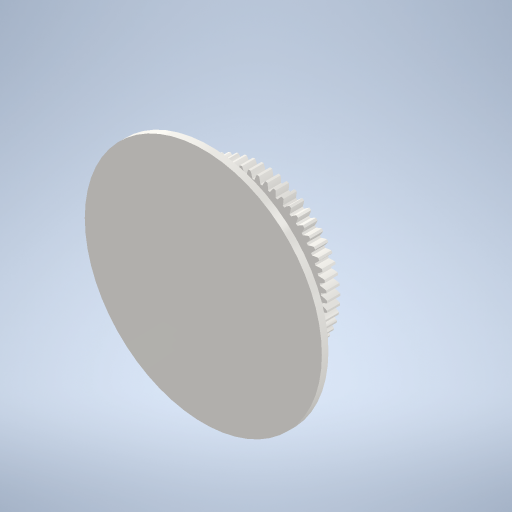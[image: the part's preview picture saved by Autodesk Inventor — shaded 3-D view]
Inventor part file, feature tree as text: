
AUTODESK INVENTOR PART (.ipt)
format: ipt  version: 2023 (Build 270158000, 158)  size: 658,944 bytes
history: native  units: mm (DEFAULTED — no unit token found)
features: sketch x4, extrude x3, plane x3, other x3, projected_geometry x2
ambient origin geometry x8: Origin, YZ Plane, XZ Plane, XY Plane, X Axis, Y Axis, Z Axis, Center Point
bodies: Solid1 (feature_tree)
feature tree (15):
  extrude  "Extrusion1"  Depth=10.0mm TaperAngle=0.0deg
  plane  "Work Plane2"
  plane  "Work Plane8"
  plane  "Work Plane9"
  other  "Spur Gear"
  extrude  "Extrusion2"  Depth=10.0mm TaperAngle=0.0deg
  extrude  "Extrusion4"  Depth=80.0mm TaperAngle=0.0deg
  sketch  "Sketch1"  dims[d0=118.0mm d1=10.0mm d2=0.0mm]
  sketch  "Sketch2"  dims[d3=114.0mm d4=10.0mm d5=0.0mm]
  other  "Srf1"
  sketch  "Sketch3"  dims[d16=80.0mm d17=0.0mm d34=0.551157mm]
  projected_geometry  "Projected Loop1"
  sketch  "Sketch5"  dims[d39=0.0mm d41=0.0mm d43=80.0mm d46=80.0mm d47=0.0mm d48=0.0mm d49=9.8mm d50=35.0mm d51=0.0mm d55=40.0mm d56=0.0mm d57=180.0mm d58=5.0mm d59=0.0mm d53=0.5mm d54=0.872665mm]
  projected_geometry  "Projected Loop3"
  other  "Pitch Diameter"
